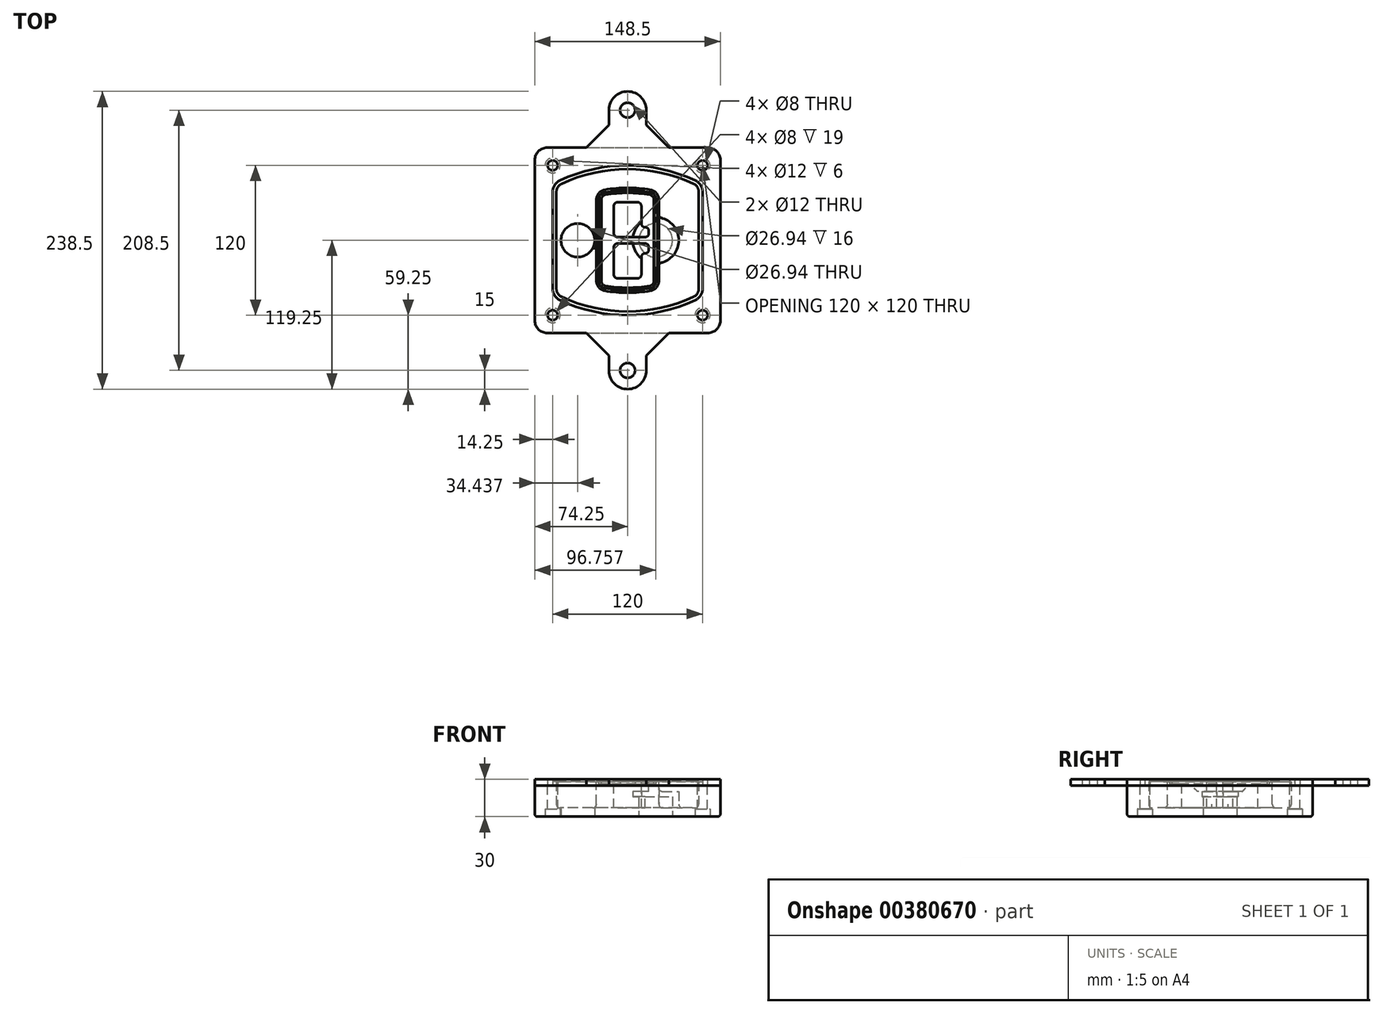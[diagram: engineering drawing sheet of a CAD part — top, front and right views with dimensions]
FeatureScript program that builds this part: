
annotation { "Feature Type Name" : "Feature", "Feature Type Description" : "" }
export const myFeature = defineFeature(function(context is Context, id is Id, definition is map)
    precondition{}
    {
        {
            var Q0;
            Q0=qCreatedBy(makeId("Top.planeOp"),FACE);
            var sketch = newSketch(context, id + "F0", { "sketchPlane" : qUnion([Q0])});
            skPoint(sketch, "E0.rect.middle", {"position": v(0, 0) * mm});
            skLineSegment(sketch, "E1.bottom", {"start": v(-64.25, -74.25) * mm, "end": v(64.25, -74.25) * mm});
            skLineSegment(sketch, "E1.top", {"start": v(-64.25, 74.25) * mm, "end": v(64.25, 74.25) * mm});
            skLineSegment(sketch, "E1.left", {"start": v(-74.25, -64.25) * mm, "end": v(-74.25, 64.25) * mm});
            skLineSegment(sketch, "E1.right", {"start": v(74.25, -64.25) * mm, "end": v(74.25, 64.25) * mm});
            skLineSegment(sketch, "E2", {"start": v(-74.25, 74.25) * mm, "end": v(74.25, -74.25) * mm, "construction": true});
            skLineSegment(sketch, "E3", {"start": v(74.25, 74.25) * mm, "end": v(-74.25, -74.25) * mm, "construction": true});
            skCircle(sketch, "E4", {"center": v(-60, 60) * mm, "radius": 4 * mm});
            skCircle(sketch, "E5", {"center": v(60, 60) * mm, "radius": 4 * mm});
            skCircle(sketch, "E6", {"center": v(60, -60) * mm, "radius": 4 * mm});
            skCircle(sketch, "E7", {"center": v(-60, -60) * mm, "radius": 4 * mm});
            skLineSegment(sketch, "E8", {"start": v(-60, 60) * mm, "end": v(60, 60) * mm, "construction": true});
            skLineSegment(sketch, "E9", {"start": v(60, 60) * mm, "end": v(60, -60) * mm, "construction": true});
            skLineSegment(sketch, "E10", {"start": v(60, -60) * mm, "end": v(-60, -60) * mm, "construction": true});
            skLineSegment(sketch, "E11", {"start": v(-60, -60) * mm, "end": v(-60, 60) * mm, "construction": true});
            skLineSegment(sketch, "E12", {"start": v(-60, 38.83) * mm, "end": v(-60, -38.83) * mm});
            skLineSegment(sketch, "E13", {"start": v(60, 38.83) * mm, "end": v(60, -38.83) * mm});
            skArc(sketch, "E14", {"start": v(54.26, 47.88) * mm, "mid": v(0, 60) * mm, "end": v(-54.26, 47.88) * mm});
            skArc(sketch, "E15", {"start": v(-54.26, -47.88) * mm, "mid": v(0, -60) * mm, "end": v(54.26, -47.88) * mm});
            skLineSegment(sketch, "E16", {"start": v(-60, 0) * mm, "end": v(60, 0) * mm, "construction": true});
            skPoint(sketch, "E17.visualSharp", {"position": v(-60, -45) * mm});
            skArc(sketch, "E17.filletArc", {"start": v(-60, -38.83) * mm, "mid": v(-58.44, -44.2) * mm, "end": v(-54.26, -47.88) * mm});
            skPoint(sketch, "E18.visualSharp", {"position": v(-60, 45) * mm});
            skArc(sketch, "E18.filletArc", {"start": v(-54.26, 47.88) * mm, "mid": v(-58.44, 44.2) * mm, "end": v(-60, 38.83) * mm});
            skPoint(sketch, "E19.visualSharp", {"position": v(60, 45) * mm});
            skArc(sketch, "E19.filletArc", {"start": v(60, 38.83) * mm, "mid": v(58.44, 44.2) * mm, "end": v(54.26, 47.88) * mm});
            skPoint(sketch, "E20.visualSharp", {"position": v(60, -45) * mm});
            skArc(sketch, "E20.filletArc", {"start": v(54.26, -47.88) * mm, "mid": v(58.44, -44.2) * mm, "end": v(60, -38.83) * mm});
            skPoint(sketch, "E21.visualSharp", {"position": v(-74.25, 74.25) * mm});
            skArc(sketch, "E21.filletArc", {"start": v(-64.25, 74.25) * mm, "mid": v(-71.32, 71.32) * mm, "end": v(-74.25, 64.25) * mm});
            skPoint(sketch, "E22.visualSharp", {"position": v(74.25, 74.25) * mm});
            skArc(sketch, "E22.filletArc", {"start": v(74.25, 64.25) * mm, "mid": v(71.32, 71.32) * mm, "end": v(64.25, 74.25) * mm});
            skPoint(sketch, "E23.visualSharp", {"position": v(74.25, -74.25) * mm});
            skArc(sketch, "E23.filletArc", {"start": v(64.25, -74.25) * mm, "mid": v(71.32, -71.32) * mm, "end": v(74.25, -64.25) * mm});
            skPoint(sketch, "E24.visualSharp", {"position": v(-74.25, -74.25) * mm});
            skArc(sketch, "E24.filletArc", {"start": v(-74.25, -64.25) * mm, "mid": v(-71.32, -71.32) * mm, "end": v(-64.25, -74.25) * mm});
            skArc(sketch, "E25.0", {"start": v(57, 38.83) * mm, "mid": v(55.9, 42.58) * mm, "end": v(52.98, 45.17) * mm});
            skLineSegment(sketch, "E25.1", {"start": v(57, 38.83) * mm, "end": v(57, -38.83) * mm});
            skArc(sketch, "E25.2", {"start": v(52.98, -45.17) * mm, "mid": v(55.9, -42.58) * mm, "end": v(57, -38.83) * mm});
            skArc(sketch, "E25.3", {"start": v(-52.98, -45.17) * mm, "mid": v(0, -57) * mm, "end": v(52.98, -45.17) * mm});
            skArc(sketch, "E25.4", {"start": v(-57, -38.83) * mm, "mid": v(-55.9, -42.58) * mm, "end": v(-52.98, -45.17) * mm});
            skArc(sketch, "E25.5", {"start": v(52.98, 45.17) * mm, "mid": v(0, 57) * mm, "end": v(-52.98, 45.17) * mm});
            skLineSegment(sketch, "E25.6", {"start": v(-57, 38.83) * mm, "end": v(-57, -38.83) * mm});
            skArc(sketch, "E25.7", {"start": v(-52.98, 45.17) * mm, "mid": v(-55.9, 42.58) * mm, "end": v(-57, 38.83) * mm});
            skArc(sketch, "E26.0", {"start": v(-55.96, 51.5) * mm, "mid": v(-61.82, 46.33) * mm, "end": v(-64, 38.83) * mm});
            skArc(sketch, "E26.1", {"start": v(55.96, 51.5) * mm, "mid": v(0, 64) * mm, "end": v(-55.96, 51.5) * mm});
            skArc(sketch, "E26.2", {"start": v(64, 38.83) * mm, "mid": v(61.82, 46.33) * mm, "end": v(55.96, 51.5) * mm});
            skLineSegment(sketch, "E26.3", {"start": v(64, 38.83) * mm, "end": v(64, -38.83) * mm});
            skArc(sketch, "E26.4", {"start": v(55.96, -51.5) * mm, "mid": v(61.82, -46.33) * mm, "end": v(64, -38.83) * mm});
            skLineSegment(sketch, "E26.5", {"start": v(-64, 38.83) * mm, "end": v(-64, -38.83) * mm});
            skArc(sketch, "E26.6", {"start": v(-55.96, -51.5) * mm, "mid": v(0, -64) * mm, "end": v(55.96, -51.5) * mm});
            skArc(sketch, "E26.7", {"start": v(-64, -38.83) * mm, "mid": v(-61.82, -46.33) * mm, "end": v(-55.96, -51.5) * mm});
            skSolve(sketch);
        }
        {
            var Q0;
            Q0=makeQuery(id+"F0.imprint","IMPRINT",FACE,{"disambiguationData":[TD([[makeQuery(id+"F0.imprint","IMPRINT",EDGE,{"derivedFrom":sQuery(id+"F0.wireOp",EDGE,"E1.bottom")}),1.0]])]});
            var Q1;
            Q1=makeQuery(id+"F0.imprint","IMPRINT",FACE,{"disambiguationData":[TD([[makeQuery(id+"F0.imprint","IMPRINT",EDGE,{"derivedFrom":sQuery(id+"F0.wireOp",EDGE,"E12")}),1.0]])]});
            var Q2;
            Q2=makeQuery(id+"F0.imprint","IMPRINT",FACE,{"disambiguationData":[TD([[makeQuery(id+"F0.imprint","IMPRINT",EDGE,{"derivedFrom":sQuery(id+"F0.wireOp",EDGE,"E25.0")}),1.0]])]});
            var Q3;
            Q3=makeQuery(id+"F0.imprint","IMPRINT",FACE,{"disambiguationData":[TD([[makeQuery(id+"F0.imprint","IMPRINT",EDGE,{"derivedFrom":sQuery(id+"F0.wireOp",EDGE,"E12")}),-1.0]])]});
            extrude(context, id + "F1", {"entities" : qUnion([Q0, Q1, Q2, Q3]), "oppositeDirection" : true, "depth" : 25 * mm});
        }
        {
            var Q0;
            Q0=makeQuery(id+"F0.imprint","IMPRINT",FACE,{"disambiguationData":[TD([[makeQuery(id+"F0.imprint","IMPRINT",EDGE,{"derivedFrom":sQuery(id+"F0.wireOp",EDGE,"E12")}),1.0]])]});
            extrude(context, id + "F2", {"entities" : qUnion([Q0]), "operationType" : NewBodyOperationType.ADD, "depth" : 3 * mm});
        }
        {
            var Q0;
            Q0=makeQuery(id+"F0.imprint","IMPRINT",FACE,{"disambiguationData":[TD([[makeQuery(id+"F0.imprint","IMPRINT",EDGE,{"derivedFrom":sQuery(id+"F0.wireOp",EDGE,"E25.0")}),1.0]])]});
            extrude(context, id + "F3", {"entities" : qUnion([Q0]), "operationType" : NewBodyOperationType.REMOVE, "oppositeDirection" : true, "depth" : 18 * mm});
        }
        {
            var Q0;
            Q0=makeQuery(id+"F2.opExtrude","CAP_FACE",FACE,{"disambiguationData":[OSD([sQuery(id+"F0.wireOp",EDGE,"E12"),sQuery(id+"F0.wireOp",EDGE,"E13"),sQuery(id+"F0.wireOp",EDGE,"E14"),sQuery(id+"F0.wireOp",EDGE,"E15"),sQuery(id+"F0.wireOp",EDGE,"E17.filletArc"),sQuery(id+"F0.wireOp",EDGE,"E18.filletArc"),sQuery(id+"F0.wireOp",EDGE,"E19.filletArc"),sQuery(id+"F0.wireOp",EDGE,"E20.filletArc"),sQuery(id+"F0.wireOp",EDGE,"E25.0"),sQuery(id+"F0.wireOp",EDGE,"E25.1"),sQuery(id+"F0.wireOp",EDGE,"E25.2"),sQuery(id+"F0.wireOp",EDGE,"E25.3"),sQuery(id+"F0.wireOp",EDGE,"E25.4"),sQuery(id+"F0.wireOp",EDGE,"E25.5"),sQuery(id+"F0.wireOp",EDGE,"E25.6"),sQuery(id+"F0.wireOp",EDGE,"E25.7")])],"isStart":false});
            var sketch = newSketch(context, id + "F4", { "sketchPlane" : qUnion([Q0])});
            skArc(sketch, "E27.0", {"start": v(-18.34, -40.45) * mm, "mid": v(0, -42) * mm, "end": v(18.34, -40.45) * mm});
            skArc(sketch, "E28.0", {"start": v(18.34, 40.45) * mm, "mid": v(0, 42) * mm, "end": v(-18.34, 40.45) * mm});
            skLineSegment(sketch, "E29", {"start": v(-25, 32.57) * mm, "end": v(-25, -32.57) * mm});
            skLineSegment(sketch, "E30", {"start": v(25, 32.57) * mm, "end": v(25, -32.57) * mm});
            skLineSegment(sketch, "E31", {"start": v(-25, 39.1) * mm, "end": v(25, 39.1) * mm, "construction": true});
            skLineSegment(sketch, "E32", {"start": v(-25, -39.1) * mm, "end": v(25, -39.1) * mm, "construction": true});
            skPoint(sketch, "E33.visualSharp", {"position": v(-25, 39.1) * mm});
            skArc(sketch, "E33.filletArc", {"start": v(-18.34, 40.45) * mm, "mid": v(-23.11, 37.73) * mm, "end": v(-25, 32.57) * mm});
            skPoint(sketch, "E34.visualSharp", {"position": v(25, 39.1) * mm});
            skArc(sketch, "E34.filletArc", {"start": v(25, 32.57) * mm, "mid": v(23.11, 37.73) * mm, "end": v(18.34, 40.45) * mm});
            skPoint(sketch, "E35.visualSharp", {"position": v(25, -39.1) * mm});
            skArc(sketch, "E35.filletArc", {"start": v(18.34, -40.45) * mm, "mid": v(23.11, -37.73) * mm, "end": v(25, -32.57) * mm});
            skPoint(sketch, "E36.visualSharp", {"position": v(-25, -39.1) * mm});
            skArc(sketch, "E36.filletArc", {"start": v(-25, -32.57) * mm, "mid": v(-23.11, -37.73) * mm, "end": v(-18.34, -40.45) * mm});
            skArc(sketch, "E37.0", {"start": v(52.98, 45.17) * mm, "mid": v(0, 57) * mm, "end": v(-52.98, 45.17) * mm});
            skArc(sketch, "E37.1", {"start": v(-52.98, 45.17) * mm, "mid": v(-55.9, 42.58) * mm, "end": v(-57, 38.83) * mm});
            skLineSegment(sketch, "E37.2", {"start": v(-57, 38.83) * mm, "end": v(-57, -38.83) * mm});
            skArc(sketch, "E37.3", {"start": v(-57, -38.83) * mm, "mid": v(-55.9, -42.58) * mm, "end": v(-52.98, -45.17) * mm});
            skArc(sketch, "E37.4", {"start": v(-52.98, -45.17) * mm, "mid": v(0, -57) * mm, "end": v(52.98, -45.17) * mm});
            skArc(sketch, "E37.5", {"start": v(52.98, -45.17) * mm, "mid": v(55.9, -42.58) * mm, "end": v(57, -38.83) * mm});
            skLineSegment(sketch, "E37.6", {"start": v(57, 38.83) * mm, "end": v(57, -38.83) * mm});
            skArc(sketch, "E37.7", {"start": v(57, 38.83) * mm, "mid": v(55.9, 42.58) * mm, "end": v(52.98, 45.17) * mm});
            skLineSegment(sketch, "E38.0", {"start": v(23, 32.57) * mm, "end": v(23, -32.57) * mm});
            skArc(sketch, "E38.1", {"start": v(18, -38.48) * mm, "mid": v(21.58, -36.44) * mm, "end": v(23, -32.57) * mm});
            skArc(sketch, "E38.2", {"start": v(-18, -38.48) * mm, "mid": v(0, -40) * mm, "end": v(18, -38.48) * mm});
            skArc(sketch, "E38.3", {"start": v(-23, -32.57) * mm, "mid": v(-21.58, -36.44) * mm, "end": v(-18, -38.48) * mm});
            skLineSegment(sketch, "E38.4", {"start": v(-23, 32.57) * mm, "end": v(-23, -32.57) * mm});
            skArc(sketch, "E38.5", {"start": v(23, 32.57) * mm, "mid": v(21.58, 36.44) * mm, "end": v(18, 38.48) * mm});
            skArc(sketch, "E38.6", {"start": v(-18, 38.48) * mm, "mid": v(-21.58, 36.44) * mm, "end": v(-23, 32.57) * mm});
            skArc(sketch, "E38.7", {"start": v(18, 38.48) * mm, "mid": v(0, 40) * mm, "end": v(-18, 38.48) * mm});
            skArc(sketch, "E39.0", {"start": v(21, 32.57) * mm, "mid": v(20.06, 35.15) * mm, "end": v(17.67, 36.5) * mm});
            skLineSegment(sketch, "E39.1", {"start": v(21, 32.57) * mm, "end": v(21, -32.57) * mm});
            skArc(sketch, "E39.2", {"start": v(17.67, -36.5) * mm, "mid": v(20.06, -35.15) * mm, "end": v(21, -32.57) * mm});
            skArc(sketch, "E39.3", {"start": v(-17.67, -36.5) * mm, "mid": v(0, -38) * mm, "end": v(17.67, -36.5) * mm});
            skArc(sketch, "E39.4", {"start": v(-21, -32.57) * mm, "mid": v(-20.06, -35.15) * mm, "end": v(-17.67, -36.5) * mm});
            skArc(sketch, "E39.5", {"start": v(17.67, 36.5) * mm, "mid": v(0, 38) * mm, "end": v(-17.67, 36.5) * mm});
            skLineSegment(sketch, "E39.6", {"start": v(-21, 32.57) * mm, "end": v(-21, -32.57) * mm});
            skArc(sketch, "E39.7", {"start": v(-17.67, 36.5) * mm, "mid": v(-20.06, 35.15) * mm, "end": v(-21, 32.57) * mm});
            skLineSegment(sketch, "E40", {"start": v(-25, 0) * mm, "end": v(25, 0) * mm, "construction": true});
            skLineSegment(sketch, "E41", {"start": v(-11, 5.5) * mm, "end": v(-11, 27.5) * mm});
            skLineSegment(sketch, "E42", {"start": v(-8, 30.5) * mm, "end": v(8, 30.5) * mm});
            skLineSegment(sketch, "E43", {"start": v(11, 27.5) * mm, "end": v(11, 13.5) * mm});
            skLineSegment(sketch, "E44", {"start": v(14, 10.5) * mm, "end": v(14, 10.5) * mm});
            skLineSegment(sketch, "E45", {"start": v(17, 7.5) * mm, "end": v(17, 5.5) * mm});
            skLineSegment(sketch, "E46", {"start": v(14, 2.5) * mm, "end": v(-8, 2.5) * mm});
            skPoint(sketch, "E47.visualSharp", {"position": v(-11, 30.5) * mm});
            skArc(sketch, "E47.filletArc", {"start": v(-8, 30.5) * mm, "mid": v(-10.12, 29.62) * mm, "end": v(-11, 27.5) * mm});
            skPoint(sketch, "E48.visualSharp", {"position": v(11, 30.5) * mm});
            skArc(sketch, "E48.filletArc", {"start": v(11, 27.5) * mm, "mid": v(10.12, 29.62) * mm, "end": v(8, 30.5) * mm});
            skPoint(sketch, "E49.visualSharp", {"position": v(11, 10.5) * mm});
            skArc(sketch, "E49.filletArc", {"start": v(11, 13.5) * mm, "mid": v(11.88, 11.38) * mm, "end": v(14, 10.5) * mm});
            skPoint(sketch, "E50.visualSharp", {"position": v(17, 10.5) * mm});
            skArc(sketch, "E50.filletArc", {"start": v(17, 7.5) * mm, "mid": v(16.12, 9.62) * mm, "end": v(14, 10.5) * mm});
            skPoint(sketch, "E51.visualSharp", {"position": v(17, 2.5) * mm});
            skArc(sketch, "E51.filletArc", {"start": v(14, 2.5) * mm, "mid": v(16.12, 3.38) * mm, "end": v(17, 5.5) * mm});
            skPoint(sketch, "E52.visualSharp", {"position": v(-11, 2.5) * mm});
            skArc(sketch, "E52.filletArc", {"start": v(-11, 5.5) * mm, "mid": v(-10.12, 3.38) * mm, "end": v(-8, 2.5) * mm});
            skLineSegment(sketch, "E53.0.MirrorCS", {"start": v(14, -2.5) * mm, "end": v(-8, -2.5) * mm});
            skArc(sketch, "E54.0.MirrorCS", {"start": v(-11, -5.5) * mm, "mid": v(-10.12, -3.38) * mm, "end": v(-8, -2.5) * mm});
            skLineSegment(sketch, "E55.0.MirrorCS", {"start": v(-11, -5.5) * mm, "end": v(-11, -27.5) * mm});
            skArc(sketch, "E56.0.MirrorCS", {"start": v(-8, -30.5) * mm, "mid": v(-10.12, -29.62) * mm, "end": v(-11, -27.5) * mm});
            skLineSegment(sketch, "E57.0.MirrorCS", {"start": v(-8, -30.5) * mm, "end": v(8, -30.5) * mm});
            skArc(sketch, "E58.0.MirrorCS", {"start": v(11, -27.5) * mm, "mid": v(10.12, -29.62) * mm, "end": v(8, -30.5) * mm});
            skLineSegment(sketch, "E59.0.MirrorCS", {"start": v(11, -27.5) * mm, "end": v(11, -13.5) * mm});
            skArc(sketch, "E60.0.MirrorCS", {"start": v(11, -13.5) * mm, "mid": v(11.88, -11.38) * mm, "end": v(14, -10.5) * mm});
            skArc(sketch, "E61.0.MirrorCS", {"start": v(17, -7.5) * mm, "mid": v(16.12, -9.62) * mm, "end": v(14, -10.5) * mm});
            skLineSegment(sketch, "E62.0.MirrorCS", {"start": v(17, -7.5) * mm, "end": v(17, -5.5) * mm});
            skArc(sketch, "E63.0.MirrorCS", {"start": v(14, -2.5) * mm, "mid": v(16.12, -3.38) * mm, "end": v(17, -5.5) * mm});
            skSolve(sketch);
        }
        {
            var Q0;
            Q0=makeQuery(id+"F4.imprint","IMPRINT",FACE,{"disambiguationData":[TD([[makeQuery(id+"F4.imprint","IMPRINT",EDGE,{"derivedFrom":sQuery(id+"F4.wireOp",EDGE,"E27.0")}),1.0]])]});
            var Q1;
            Q1=makeQuery(id+"F4.imprint","IMPRINT",FACE,{"disambiguationData":[TD([[makeQuery(id+"F4.imprint","IMPRINT",EDGE,{"derivedFrom":sQuery(id+"F4.wireOp",EDGE,"E38.0")}),-1.0]])]});
            var Q2;
            Q2=makeQuery(id+"F4.imprint","IMPRINT",FACE,{"disambiguationData":[TD([[makeQuery(id+"F4.imprint","IMPRINT",EDGE,{"derivedFrom":sQuery(id+"F4.wireOp",EDGE,"E39.0")}),1.0]])]});
            extrude(context, id + "F5", {"entities" : qUnion([Q0, Q1, Q2]), "operationType" : NewBodyOperationType.ADD, "endBound" : BoundingType.UP_TO_NEXT, "oppositeDirection" : true, "depth" : 25 * mm});
        }
        {
            var Q0;
            Q0=makeQuery(id+"F4.imprint","IMPRINT",FACE,{"disambiguationData":[TD([[makeQuery(id+"F4.imprint","IMPRINT",EDGE,{"derivedFrom":sQuery(id+"F4.wireOp",EDGE,"E38.0")}),-1.0]])]});
            extrude(context, id + "F6", {"entities" : qUnion([Q0]), "operationType" : NewBodyOperationType.REMOVE, "oppositeDirection" : true, "depth" : 2 * mm});
        }
        {
            var Q0;
            Q0=makeQuery(id+"F1.opExtrude","CAP_FACE",FACE,{"disambiguationData":[OSD([sQuery(id+"F0.wireOp",EDGE,"E1.bottom"),sQuery(id+"F0.wireOp",EDGE,"E1.top"),sQuery(id+"F0.wireOp",EDGE,"E1.left"),sQuery(id+"F0.wireOp",EDGE,"E1.right"),sQuery(id+"F0.wireOp",EDGE,"E4"),sQuery(id+"F0.wireOp",EDGE,"E5"),sQuery(id+"F0.wireOp",EDGE,"E6"),sQuery(id+"F0.wireOp",EDGE,"E7"),sQuery(id+"F0.wireOp",EDGE,"E21.filletArc"),sQuery(id+"F0.wireOp",EDGE,"E22.filletArc"),sQuery(id+"F0.wireOp",EDGE,"E23.filletArc"),sQuery(id+"F0.wireOp",EDGE,"E24.filletArc")])],"isStart":false});
            var sketch = newSketch(context, id + "F7", { "sketchPlane" : qUnion([Q0])});
            skCircle(sketch, "E64", {"center": v(22.5, 0) * mm, "radius": 13.47 * mm});
            skCircle(sketch, "E65", {"center": v(-39.81, 0) * mm, "radius": 13.47 * mm});
            skLineSegment(sketch, "E66", {"start": v(74.25, 0) * mm, "end": v(-74.25, 0) * mm});
            skCircle(sketch, "E67", {"center": v(22.5, 0) * mm, "radius": 18.47 * mm});
            skCircle(sketch, "E68", {"center": v(60, -60) * mm, "radius": 6 * mm});
            skCircle(sketch, "E69", {"center": v(-60, -60) * mm, "radius": 6 * mm});
            skCircle(sketch, "E70", {"center": v(-60, 60) * mm, "radius": 6 * mm});
            skCircle(sketch, "E71", {"center": v(60, 60) * mm, "radius": 6 * mm});
            skSolve(sketch);
        }
        {
            var Q0;
            {var subQ1=sQuery(id+"F7.wireOp",EDGE,"E66");var subQ4=sQuery(id+"F7.wireOp",EDGE,"E64");var subQ6=makeQuery(id+"F7.imprint","INTERSECT",VERTEX,{"disambiguationData":[OD(0.0)],"derivedFrom":[subQ4,subQ1]});Q0=makeQuery(id+"F7.imprint","IMPRINT",FACE,{"disambiguationData":[TD([[makeQuery(id+"F7.imprint","IMPRINT",EDGE,{"disambiguationData":[TD([[subQ6,-1.0]])],"derivedFrom":subQ4}),-1.0]])]});}
            var Q1;
            {var subQ0=sQuery(id+"F7.wireOp",EDGE,"E66");var subQ1=sQuery(id+"F7.wireOp",EDGE,"E64");var subQ3=makeQuery(id+"F7.imprint","INTERSECT",VERTEX,{"disambiguationData":[OD(0.0)],"derivedFrom":[subQ1,subQ0]});Q1=makeQuery(id+"F7.imprint","IMPRINT",FACE,{"disambiguationData":[TD([[makeQuery(id+"F7.imprint","IMPRINT",EDGE,{"disambiguationData":[TD([[subQ3,-1.0]])],"derivedFrom":subQ1}),1.0]])]});}
            var Q2;
            {var subQ0=sQuery(id+"F7.wireOp",EDGE,"E66");var subQ1=sQuery(id+"F7.wireOp",EDGE,"E64");var subQ3=makeQuery(id+"F7.imprint","INTERSECT",VERTEX,{"disambiguationData":[OD(0.0)],"derivedFrom":[subQ1,subQ0]});Q2=makeQuery(id+"F7.imprint","IMPRINT",FACE,{"disambiguationData":[TD([[makeQuery(id+"F7.imprint","IMPRINT",EDGE,{"disambiguationData":[TD([[subQ3,1.0]])],"derivedFrom":subQ1}),1.0]])]});}
            var Q3;
            {var subQ1=sQuery(id+"F7.wireOp",EDGE,"E66");var subQ4=sQuery(id+"F7.wireOp",EDGE,"E64");var subQ6=makeQuery(id+"F7.imprint","INTERSECT",VERTEX,{"disambiguationData":[OD(0.0)],"derivedFrom":[subQ4,subQ1]});Q3=makeQuery(id+"F7.imprint","IMPRINT",FACE,{"disambiguationData":[TD([[makeQuery(id+"F7.imprint","IMPRINT",EDGE,{"disambiguationData":[TD([[subQ6,1.0]])],"derivedFrom":subQ4}),-1.0]])]});}
            extrude(context, id + "F8", {"entities" : qUnion([Q0, Q1, Q2, Q3]), "operationType" : NewBodyOperationType.ADD, "oppositeDirection" : true, "depth" : 20 * mm});
        }
        {
            var Q0;
            {var subQ0=sQuery(id+"F7.wireOp",EDGE,"E66");var subQ1=sQuery(id+"F7.wireOp",EDGE,"E64");var subQ3=makeQuery(id+"F7.imprint","INTERSECT",VERTEX,{"disambiguationData":[OD(0.0)],"derivedFrom":[subQ1,subQ0]});Q0=makeQuery(id+"F7.imprint","IMPRINT",FACE,{"disambiguationData":[TD([[makeQuery(id+"F7.imprint","IMPRINT",EDGE,{"disambiguationData":[TD([[subQ3,-1.0]])],"derivedFrom":subQ1}),1.0]])]});}
            var Q1;
            {var subQ0=sQuery(id+"F7.wireOp",EDGE,"E66");var subQ1=sQuery(id+"F7.wireOp",EDGE,"E64");var subQ3=makeQuery(id+"F7.imprint","INTERSECT",VERTEX,{"disambiguationData":[OD(0.0)],"derivedFrom":[subQ1,subQ0]});Q1=makeQuery(id+"F7.imprint","IMPRINT",FACE,{"disambiguationData":[TD([[makeQuery(id+"F7.imprint","IMPRINT",EDGE,{"disambiguationData":[TD([[subQ3,1.0]])],"derivedFrom":subQ1}),1.0]])]});}
            extrude(context, id + "F9", {"entities" : qUnion([Q0, Q1]), "operationType" : NewBodyOperationType.REMOVE, "oppositeDirection" : true, "depth" : 16 * mm});
        }
        {
            var Q0;
            {var subQ0=sQuery(id+"F7.wireOp",EDGE,"E66");var subQ1=sQuery(id+"F7.wireOp",EDGE,"E65");var subQ3=makeQuery(id+"F7.imprint","INTERSECT",VERTEX,{"disambiguationData":[OD(0.0)],"derivedFrom":[subQ1,subQ0]});Q0=makeQuery(id+"F7.imprint","IMPRINT",FACE,{"disambiguationData":[TD([[makeQuery(id+"F7.imprint","IMPRINT",EDGE,{"disambiguationData":[TD([[subQ3,-1.0]])],"derivedFrom":subQ1}),1.0]])]});}
            var Q1;
            {var subQ0=sQuery(id+"F7.wireOp",EDGE,"E66");var subQ1=sQuery(id+"F7.wireOp",EDGE,"E65");var subQ3=makeQuery(id+"F7.imprint","INTERSECT",VERTEX,{"disambiguationData":[OD(0.0)],"derivedFrom":[subQ1,subQ0]});Q1=makeQuery(id+"F7.imprint","IMPRINT",FACE,{"disambiguationData":[TD([[makeQuery(id+"F7.imprint","IMPRINT",EDGE,{"disambiguationData":[TD([[subQ3,1.0]])],"derivedFrom":subQ1}),1.0]])]});}
            extrude(context, id + "F10", {"entities" : qUnion([Q0, Q1]), "operationType" : NewBodyOperationType.REMOVE, "oppositeDirection" : true, "depth" : 25 * mm});
        }
        {
            var Q0;
            Q0=makeQuery(id+"F7.imprint","IMPRINT",FACE,{"disambiguationData":[TD([[makeQuery(id+"F7.imprint","IMPRINT",EDGE,{"derivedFrom":sQuery(id+"F7.wireOp",EDGE,"E68")}),1.0]])]});
            var Q1;
            Q1=makeQuery(id+"F7.imprint","IMPRINT",FACE,{"disambiguationData":[TD([[makeQuery(id+"F7.imprint","IMPRINT",EDGE,{"derivedFrom":makeQuery(id+"F1.opExtrude","CAP_EDGE",EDGE,{"disambiguationData":[OSD([sQuery(id+"F0.wireOp",EDGE,"E5")])],"isStart":false})}),-1.0]])]});
            var Q2;
            Q2=makeQuery(id+"F7.imprint","IMPRINT",FACE,{"disambiguationData":[TD([[makeQuery(id+"F7.imprint","IMPRINT",EDGE,{"derivedFrom":sQuery(id+"F7.wireOp",EDGE,"E69")}),1.0]])]});
            var Q3;
            Q3=makeQuery(id+"F7.imprint","IMPRINT",FACE,{"disambiguationData":[TD([[makeQuery(id+"F7.imprint","IMPRINT",EDGE,{"derivedFrom":makeQuery(id+"F1.opExtrude","CAP_EDGE",EDGE,{"disambiguationData":[OSD([sQuery(id+"F0.wireOp",EDGE,"E4")])],"isStart":false})}),-1.0]])]});
            var Q4;
            Q4=makeQuery(id+"F7.imprint","IMPRINT",FACE,{"disambiguationData":[TD([[makeQuery(id+"F7.imprint","IMPRINT",EDGE,{"derivedFrom":sQuery(id+"F7.wireOp",EDGE,"E70")}),1.0]])]});
            var Q5;
            Q5=makeQuery(id+"F7.imprint","IMPRINT",FACE,{"disambiguationData":[TD([[makeQuery(id+"F7.imprint","IMPRINT",EDGE,{"derivedFrom":makeQuery(id+"F1.opExtrude","CAP_EDGE",EDGE,{"disambiguationData":[OSD([sQuery(id+"F0.wireOp",EDGE,"E7")])],"isStart":false})}),-1.0]])]});
            var Q6;
            Q6=makeQuery(id+"F7.imprint","IMPRINT",FACE,{"disambiguationData":[TD([[makeQuery(id+"F7.imprint","IMPRINT",EDGE,{"derivedFrom":sQuery(id+"F7.wireOp",EDGE,"E71")}),1.0]])]});
            var Q7;
            Q7=makeQuery(id+"F7.imprint","IMPRINT",FACE,{"disambiguationData":[TD([[makeQuery(id+"F7.imprint","IMPRINT",EDGE,{"derivedFrom":makeQuery(id+"F1.opExtrude","CAP_EDGE",EDGE,{"disambiguationData":[OSD([sQuery(id+"F0.wireOp",EDGE,"E6")])],"isStart":false})}),-1.0]])]});
            extrude(context, id + "F11", {"entities" : qUnion([Q0, Q1, Q2, Q3, Q4, Q5, Q6, Q7]), "operationType" : NewBodyOperationType.REMOVE, "oppositeDirection" : true, "depth" : 6 * mm});
        }
        {
            var Q0;
            Q0=makeQuery(id+"F9.boolean.opBoolean","COPY",FACE,{"derivedFrom":makeQuery(id+"F9.opExtrude","CAP_FACE",FACE,{"disambiguationData":[OSD([sQuery(id+"F7.wireOp",EDGE,"E64")])],"isStart":false})});
            var sketch = newSketch(context, id + "F12", { "sketchPlane" : qUnion([Q0])});
            skArc(sketch, "E72.0", {"start": v(11, 14.45) * mm, "mid": v(6.45, 9.13) * mm, "end": v(4.2, 2.5) * mm});
            skArc(sketch, "E72.1", {"start": v(4.2, -2.5) * mm, "mid": v(6.45, -9.13) * mm, "end": v(11, -14.45) * mm});
            skLineSegment(sketch, "E73", {"start": v(4.2, -2.5) * mm, "end": v(14, -2.5) * mm});
            skLineSegment(sketch, "E74.0", {"start": v(14, 2.5) * mm, "end": v(4.2, 2.5) * mm});
            skArc(sketch, "E74.1", {"start": v(14, 2.5) * mm, "mid": v(16.12, 3.38) * mm, "end": v(17, 5.5) * mm});
            skLineSegment(sketch, "E74.2", {"start": v(17, 7.5) * mm, "end": v(17, 5.5) * mm});
            skArc(sketch, "E74.3", {"start": v(17, 7.5) * mm, "mid": v(16.12, 9.62) * mm, "end": v(14, 10.5) * mm});
            skArc(sketch, "E74.4", {"start": v(11, 13.5) * mm, "mid": v(11.88, 11.38) * mm, "end": v(14, 10.5) * mm});
            skLineSegment(sketch, "E74.5", {"start": v(11, 14.45) * mm, "end": v(11, 13.5) * mm});
            skLineSegment(sketch, "E74.7", {"start": v(14, -2.5) * mm, "end": v(4.2, -2.5) * mm});
            skArc(sketch, "E74.8", {"start": v(14, -2.5) * mm, "mid": v(16.12, -3.38) * mm, "end": v(17, -5.5) * mm});
            skLineSegment(sketch, "E74.9", {"start": v(17, -7.5) * mm, "end": v(17, -5.5) * mm});
            skArc(sketch, "E74.10", {"start": v(17, -7.5) * mm, "mid": v(16.12, -9.62) * mm, "end": v(14, -10.5) * mm});
            skArc(sketch, "E74.11", {"start": v(11, -13.5) * mm, "mid": v(11.88, -11.38) * mm, "end": v(14, -10.5) * mm});
            skLineSegment(sketch, "E74.12", {"start": v(11, -14.45) * mm, "end": v(11, -13.5) * mm});
            skPoint(sketch, "E75.orphan", {"position": v(11, -27.5) * mm});
            skPoint(sketch, "E76.orphan", {"position": v(-8, -2.5) * mm});
            skPoint(sketch, "E77.orphan", {"position": v(-8, 2.5) * mm});
            skPoint(sketch, "E78.orphan", {"position": v(11, 27.5) * mm});
            skSolve(sketch);
        }
        {
            var Q0;
            {var subQ7=sQuery(id+"F12.wireOp",EDGE,"E72.0");var subQ14=sQuery(id+"F12.wireOp",EDGE,"E72.1");var subQ16=sQuery(id+"F12.wireOp",EDGE,"E74.1");var subQ18=sQuery(id+"F12.wireOp",EDGE,"E74.8");Q0=qUnion([makeQuery(id+"F12.imprint","IMPRINT",FACE,{"disambiguationData":[TD([[makeQuery(id+"F12.imprint","IMPRINT",EDGE,{"derivedFrom":subQ7}),1.0]])]}),makeQuery(id+"F12.imprint","IMPRINT",FACE,{"disambiguationData":[TD([[makeQuery(id+"F12.imprint","IMPRINT",EDGE,{"derivedFrom":subQ14}),1.0]])]}),makeQuery(id+"F12.imprint","IMPRINT",FACE,{"disambiguationData":[TD([[makeQuery(id+"F12.imprint","IMPRINT",EDGE,{"derivedFrom":subQ16}),1.0]])]}),makeQuery(id+"F12.imprint","IMPRINT",FACE,{"disambiguationData":[TD([[makeQuery(id+"F12.imprint","IMPRINT",EDGE,{"derivedFrom":subQ18}),-1.0]])]})]);}
            var Q1;
            Q1=makeQuery(id+"F5.boolean.opBoolean","SPLIT",FACE,{"disambiguationData":[TD([makeQuery(id+"F5.opExtrude","SWEPT_FACE",FACE,{"disambiguationData":[OSD([sQuery(id+"F4.wireOp",EDGE,"E41")])]})])],"derivedFrom":makeQuery(id+"F3.boolean.opBoolean","COPY",FACE,{"derivedFrom":makeQuery(id+"F3.opExtrude","CAP_FACE",FACE,{"disambiguationData":[OSD([sQuery(id+"F0.wireOp",EDGE,"E25.0"),sQuery(id+"F0.wireOp",EDGE,"E25.1"),sQuery(id+"F0.wireOp",EDGE,"E25.2"),sQuery(id+"F0.wireOp",EDGE,"E25.3"),sQuery(id+"F0.wireOp",EDGE,"E25.4"),sQuery(id+"F0.wireOp",EDGE,"E25.5"),sQuery(id+"F0.wireOp",EDGE,"E25.6"),sQuery(id+"F0.wireOp",EDGE,"E25.7")])],"isStart":false})})});
            extrude(context, id + "F13", {"entities" : qUnion([Q0]), "operationType" : NewBodyOperationType.REMOVE, "endBound" : BoundingType.UP_TO_SURFACE, "endBoundEntityFace" : qUnion([Q1]), "depth" : 25 * mm});
        }
        {
            var Q0;
            Q0=makeQuery(id+"F3.boolean.opBoolean","COPY",EDGE,{"derivedFrom":makeQuery(id+"F3.opExtrude","CAP_EDGE",EDGE,{"disambiguationData":[OSD([sQuery(id+"F0.wireOp",EDGE,"E25.6")])],"isStart":false})});
            var Q1;
            Q1=makeQuery(id+"F8.boolean.opBoolean","INTERSECT",EDGE,{"derivedFrom":[makeQuery(id+"F5.opExtrude","SWEPT_FACE",FACE,{"disambiguationData":[OSD([sQuery(id+"F4.wireOp",EDGE,"E30")])]}),makeQuery(id+"F8.opExtrude","CAP_FACE",FACE,{"disambiguationData":[OSD([sQuery(id+"F7.wireOp",EDGE,"E67")])],"isStart":false})]});
            var Q2;
            Q2=makeQuery(id+"F8.boolean.opBoolean","INTERSECT",EDGE,{"disambiguationData":[OD(1.0)],"derivedFrom":[makeQuery(id+"F5.opExtrude","SWEPT_FACE",FACE,{"disambiguationData":[OSD([sQuery(id+"F4.wireOp",EDGE,"E30")])]}),makeQuery(id+"F8.opExtrude","SWEPT_FACE",FACE,{"disambiguationData":[OSD([sQuery(id+"F7.wireOp",EDGE,"E67")])]})]});
            var Q3;
            {var subQ0=sQuery(id+"F4.wireOp",EDGE,"E30");Q3=makeQuery(id+"F8.boolean.opBoolean","SPLIT",EDGE,{"disambiguationData":[TD([makeQuery(id+"F5.opExtrude","SWEPT_FACE",FACE,{"disambiguationData":[OSD([sQuery(id+"F4.wireOp",EDGE,"E35.filletArc")])]})])],"derivedFrom":makeQuery(id+"F5.opExtrude","CAP_EDGE",EDGE,{"disambiguationData":[OSD([subQ0])],"isStart":false})});}
            var Q4;
            {var subQ0=sQuery(id+"F0.wireOp",EDGE,"E25.7");var subQ1=sQuery(id+"F0.wireOp",EDGE,"E25.1");var subQ2=sQuery(id+"F0.wireOp",EDGE,"E25.6");var subQ3=sQuery(id+"F0.wireOp",EDGE,"E25.5");var subQ4=sQuery(id+"F0.wireOp",EDGE,"E25.4");var subQ5=sQuery(id+"F0.wireOp",EDGE,"E25.0");var subQ6=sQuery(id+"F0.wireOp",EDGE,"E25.2");var subQ7=sQuery(id+"F0.wireOp",EDGE,"E25.3");Q4=makeQuery(id+"F8.boolean.opBoolean","INTERSECT",EDGE,{"derivedFrom":[makeQuery(id+"F5.boolean.opBoolean","SPLIT",FACE,{"disambiguationData":[TD([makeQuery(id+"F2.opExtrude","SWEPT_FACE",FACE,{"disambiguationData":[OSD([subQ5])]})])],"derivedFrom":makeQuery(id+"F3.boolean.opBoolean","COPY",FACE,{"derivedFrom":makeQuery(id+"F3.opExtrude","CAP_FACE",FACE,{"disambiguationData":[OSD([subQ5,subQ1,subQ6,subQ7,subQ4,subQ3,subQ2,subQ0])],"isStart":false})})}),makeQuery(id+"F8.opExtrude","SWEPT_FACE",FACE,{"disambiguationData":[OSD([sQuery(id+"F7.wireOp",EDGE,"E67")])]})]});}
            var Q5;
            Q5=makeQuery(id+"F8.boolean.opBoolean","INTERSECT",EDGE,{"disambiguationData":[OD(0.0)],"derivedFrom":[makeQuery(id+"F5.opExtrude","SWEPT_FACE",FACE,{"disambiguationData":[OSD([sQuery(id+"F4.wireOp",EDGE,"E30")])]}),makeQuery(id+"F8.opExtrude","SWEPT_FACE",FACE,{"disambiguationData":[OSD([sQuery(id+"F7.wireOp",EDGE,"E67")])]})]});
            fillet(context, id + "F14", {"entities" : qUnion([Q0, Q1, Q2, Q3, Q4, Q5]), "radius" : 3 * mm, "tangentPropagation" : true, "allowEdgeOverflow" : false});
        }
        {
            var Q0;
            Q0=makeQuery(id+"F1.opExtrude","CAP_EDGE",EDGE,{"disambiguationData":[OSD([sQuery(id+"F0.wireOp",EDGE,"E1.bottom")])],"isStart":false});
            fillet(context, id + "F15", {"entities" : qUnion([Q0]), "radius" : 2 * mm, "tangentPropagation" : true, "allowEdgeOverflow" : false});
        }
        {
            var Q0;
            {var subQ0=sQuery(id+"F0.wireOp",EDGE,"E21.filletArc");var subQ1=sQuery(id+"F0.wireOp",EDGE,"E7");var subQ2=sQuery(id+"F0.wireOp",EDGE,"E6");var subQ3=sQuery(id+"F0.wireOp",EDGE,"E5");var subQ4=sQuery(id+"F0.wireOp",EDGE,"E4");var subQ5=sQuery(id+"F0.wireOp",EDGE,"E22.filletArc");var subQ6=sQuery(id+"F0.wireOp",EDGE,"E1.bottom");var subQ7=sQuery(id+"F0.wireOp",EDGE,"E1.right");var subQ8=sQuery(id+"F0.wireOp",EDGE,"E1.top");var subQ9=sQuery(id+"F0.wireOp",EDGE,"E1.left");var subQ10=sQuery(id+"F0.wireOp",EDGE,"E23.filletArc");var subQ11=sQuery(id+"F0.wireOp",EDGE,"E24.filletArc");Q0=makeQuery(id+"F2.boolean.opBoolean","SPLIT",FACE,{"disambiguationData":[TD([makeQuery(id+"F1.opExtrude","SWEPT_FACE",FACE,{"disambiguationData":[OSD([subQ6])]})])],"derivedFrom":makeQuery(id+"F1.opExtrude","CAP_FACE",FACE,{"disambiguationData":[OSD([subQ6,subQ8,subQ9,subQ7,subQ4,subQ3,subQ2,subQ1,subQ0,subQ5,subQ10,subQ11])],"isStart":true})});}
            var sketch = newSketch(context, id + "F16", { "sketchPlane" : qUnion([Q0])});
            skCircle(sketch, "E79", {"center": v(0, 104.25) * mm, "radius": 6 * mm});
            skPoint(sketch, "E79.centerSnap0", {"position": v(0, 74.25) * mm});
            skArc(sketch, "E80", {"start": v(15, 104.25) * mm, "mid": v(0.17, 119.25) * mm, "end": v(-15, 104.6) * mm});
            skLineSegment(sketch, "E81", {"start": v(-15, 104.6) * mm, "end": v(-15, 92.25) * mm});
            skLineSegment(sketch, "E82", {"start": v(15, 104.25) * mm, "end": v(15, 92.25) * mm});
            skLineSegment(sketch, "E83", {"start": v(-15, 92.25) * mm, "end": v(-33, 74.25) * mm});
            skLineSegment(sketch, "E84", {"start": v(15, 92.25) * mm, "end": v(33, 74.25) * mm});
            skLineSegment(sketch, "E85.MirrorCS", {"start": v(-15, -92.25) * mm, "end": v(-33, -74.25) * mm});
            skLineSegment(sketch, "E86.MirrorCS", {"start": v(-15, -104.6) * mm, "end": v(-15, -92.25) * mm});
            skArc(sketch, "E87.MirrorCS", {"start": v(15, -104.25) * mm, "mid": v(0.17, -119.25) * mm, "end": v(-15, -104.6) * mm});
            skLineSegment(sketch, "E88.MirrorCS", {"start": v(15, -104.25) * mm, "end": v(15, -92.25) * mm});
            skLineSegment(sketch, "E89.MirrorCS", {"start": v(15, -92.25) * mm, "end": v(33, -74.25) * mm});
            skCircle(sketch, "E90.MirrorC", {"center": v(0, -104.25) * mm, "radius": 6 * mm});
            skSolve(sketch);
        }
        {
            var Q0;
            Q0=makeQuery(id+"F16.imprint","IMPRINT",FACE,{"disambiguationData":[TD([[makeQuery(id+"F16.imprint","IMPRINT",EDGE,{"derivedFrom":sQuery(id+"F16.wireOp",EDGE,"E79")}),-1.0]])]});
            var Q1;
            Q1=makeQuery(id+"F16.imprint","IMPRINT",FACE,{"disambiguationData":[TD([[makeQuery(id+"F16.imprint","IMPRINT",EDGE,{"derivedFrom":makeQuery(id+"F1.opExtrude","CAP_EDGE",EDGE,{"disambiguationData":[OSD([sQuery(id+"F0.wireOp",EDGE,"E1.left")])],"isStart":true})}),-1.0]])]});
            var Q2;
            {var subQ0=sQuery(id+"F16.wireOp",EDGE,"E85.MirrorCS");Q2=makeQuery(id+"F16.imprint","IMPRINT",FACE,{"disambiguationData":[TD([[makeQuery(id+"F16.imprint","IMPRINT",EDGE,{"derivedFrom":subQ0}),-1.0]])]});}
            extrude(context, id + "F17", {"entities" : qUnion([Q0, Q1, Q2]), "depth" : 5 * mm});
        }
    });
